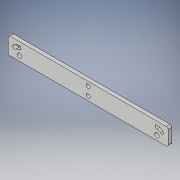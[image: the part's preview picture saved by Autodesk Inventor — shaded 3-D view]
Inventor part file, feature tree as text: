
AUTODESK INVENTOR PART (.ipt)
format: ipt  version: 2019 (Build 230136000, 136)  size: 146,944 bytes
history: native  units: in
note: dims shown in document units (in); Inventor stores cm internally (conversion verified against a paired STEP export)
features: sketch x3, extrude x2, fillet x1, hole x1
ambient origin geometry x8: Origin, YZ Plane, XZ Plane, XY Plane, X Axis, Y Axis, Z Axis, Center Point
bodies: Solid1 (feature_tree)
feature tree (7):
  extrude  "Extrusion1"  Depth=0.7087in
  extrude  "Extrusion2"  Depth=0.0787in
  fillet  "Fillet1"  Radius=6.6929in
  hole  "Hole2"  [1 undecoded]
  sketch  "Sketch1"  dims[d0=0.1575in d1=0.0in d3=0.7087in]
  sketch  "Sketch2"  dims[d10=0.1575in d11=0.0in d12=0.0787in d26=6.6929in]
  sketch  "Sketch5"  dims[d33=0.177in d34=0.2362in d35=0.332in d36=0.0787in d37=0.5635in d38=0.315in d39=0.8108in d40=0.1969in d41=0.1495in d42=0.1495in d43=0.5906in d44=0.4724in d45=0.1969in]
note: 1 required parameter value undecoded (feature->parameter linkage not recoverable at this tier; creation-order binding heuristic only, values carry confidence <= 0.55)
